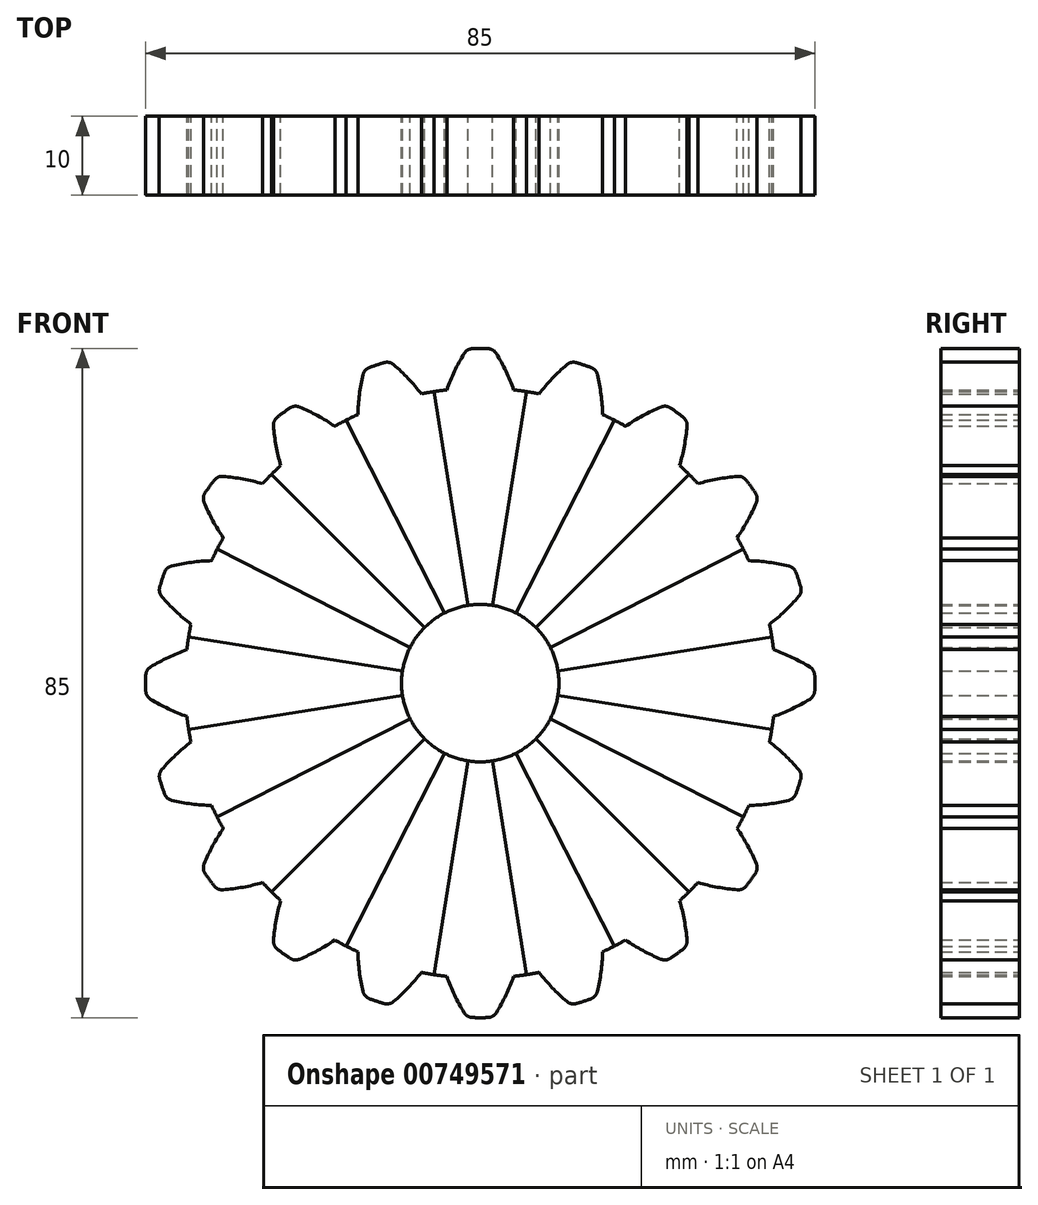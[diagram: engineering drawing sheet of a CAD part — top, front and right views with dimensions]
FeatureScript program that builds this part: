
annotation { "Feature Type Name" : "Feature", "Feature Type Description" : "" }
export const myFeature = defineFeature(function(context is Context, id is Id, definition is map)
    precondition{}
    {
        {
            var Q0;
            Q0=qCreatedBy(makeId("Front.planeOp"),FACE);
            var sketch = newSketch(context, id + "F0", { "sketchPlane" : qUnion([Q0])});
            skCircle(sketch, "E0", {"center": v(0, 0) * mm, "radius": 37.5 * mm, "construction": true});
            skArc(sketch, "E1", {"start": v(1.56, 9.88) * mm, "mid": v(0, 10) * mm, "end": v(-1.56, 9.88) * mm});
            skCircle(sketch, "E2", {"center": v(0, 0) * mm, "radius": 40 * mm, "construction": true});
            skCircle(sketch, "E3", {"center": v(0, 0) * mm, "radius": 42.5 * mm, "construction": true});
            skLineSegment(sketch, "E4", {"start": v(0, 0) * mm, "end": v(0, 42.5) * mm, "construction": true});
            skLineSegment(sketch, "E5", {"start": v(0, 0) * mm, "end": v(1.67, 42.47) * mm, "construction": true});
            skLineSegment(sketch, "E6", {"start": v(0, 0) * mm, "end": v(4.81, 42.23) * mm, "construction": true});
            skLineSegment(sketch, "E7", {"start": v(0, 0) * mm, "end": v(6.65, 41.98) * mm, "construction": true});
            skArc(sketch, "E8", {"start": v(5.87, 37.04) * mm, "mid": v(5.06, 37.16) * mm, "end": v(4.25, 37.26) * mm});
            skArc(sketch, "E9", {"start": v(0.97, 42.49) * mm, "mid": v(0.48, 42.5) * mm, "end": v(0, 42.5) * mm});
            skArc(sketch, "E10", {"start": v(4.25, 37.26) * mm, "mid": v(3.26, 39.62) * mm, "end": v(2.05, 41.87) * mm});
            skArc(sketch, "E11.MirrorCS", {"start": v(-0.97, 42.49) * mm, "mid": v(-0.48, 42.5) * mm, "end": v(0, 42.5) * mm});
            skArc(sketch, "E12.MirrorCS", {"start": v(-4.25, 37.26) * mm, "mid": v(-3.26, 39.62) * mm, "end": v(-2.05, 41.87) * mm});
            skArc(sketch, "E13.MirrorCS", {"start": v(-5.87, 37.04) * mm, "mid": v(-5.06, 37.16) * mm, "end": v(-4.25, 37.26) * mm});
            skLineSegment(sketch, "E14", {"start": v(-1.56, 9.88) * mm, "end": v(-5.87, 37.04) * mm});
            skLineSegment(sketch, "E15", {"start": v(1.56, 9.88) * mm, "end": v(5.87, 37.04) * mm});
            skPoint(sketch, "E16.visualSharp", {"position": v(1.67, 42.47) * mm});
            skArc(sketch, "E16.filletArc", {"start": v(2.05, 41.87) * mm, "mid": v(1.59, 42.32) * mm, "end": v(0.97, 42.49) * mm});
            skPoint(sketch, "E17.visualSharp", {"position": v(-1.67, 42.47) * mm});
            skArc(sketch, "E17.filletArc", {"start": v(-0.97, 42.49) * mm, "mid": v(-1.59, 42.32) * mm, "end": v(-2.05, 41.87) * mm});
            skSolve(sketch);
        }
        {
            var Q0;
            Q0 = qSketchRegion(id + "F0", true);
            extrude(context, id + "F1", {"entities" : qUnion([Q0]), "depth" : 10 * mm, "offsetDistance" : 25 * mm});
        }
        {
            var Q0;
            Q0=makeQuery(id+"F1.opExtrude","SWEPT_BODY",BODY,{"disambiguationData":[OSD([sQuery(id+"F0.wireOp",EDGE,"E1"),sQuery(id+"F0.wireOp",EDGE,"E8"),sQuery(id+"F0.wireOp",EDGE,"E9"),sQuery(id+"F0.wireOp",EDGE,"E10"),sQuery(id+"F0.wireOp",EDGE,"E11.MirrorCS"),sQuery(id+"F0.wireOp",EDGE,"E12.MirrorCS"),sQuery(id+"F0.wireOp",EDGE,"E13.MirrorCS"),sQuery(id+"F0.wireOp",EDGE,"E14"),sQuery(id+"F0.wireOp",EDGE,"E15")])]});
            var Q1;
            Q1=makeQuery(id+"F1.opExtrude","SWEPT_FACE",FACE,{"disambiguationData":[OSD([sQuery(id+"F0.wireOp",EDGE,"E1")])]});
            circularPattern(context, id + "F2", {"entities" : qUnion([Q0]), "axis" : qUnion([Q1]), "angle" : 360 * degree, "instanceCount" : 20, "equalSpace" : true, "isCentered" : true});
        }
    });
